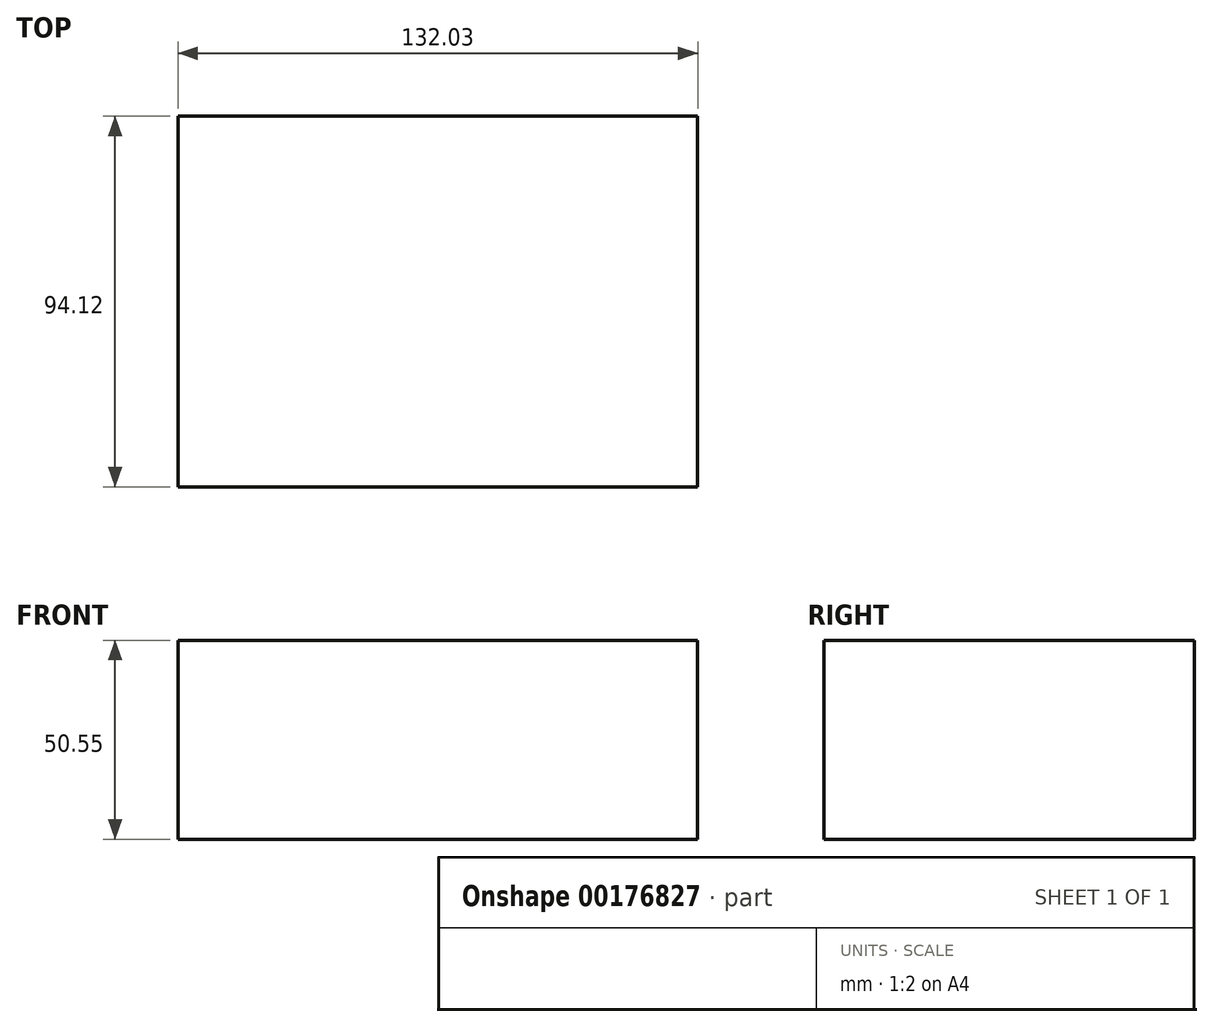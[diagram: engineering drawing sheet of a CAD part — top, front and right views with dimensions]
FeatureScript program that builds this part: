
annotation { "Feature Type Name" : "Feature", "Feature Type Description" : "" }
export const myFeature = defineFeature(function(context is Context, id is Id, definition is map)
    precondition{}
    {
        {
            var Q0;
            Q0=qCreatedBy(makeId("Top.planeOp"),FACE);
            var sketch = newSketch(context, id + "F0", { "sketchPlane" : qUnion([Q0])});
            skLineSegment(sketch, "E0.bottom", {"start": v(-87.33, 69.61) * mm, "end": v(44.7, 69.61) * mm});
            skLineSegment(sketch, "E0.top", {"start": v(-87.33, -24.5) * mm, "end": v(44.7, -24.5) * mm});
            skLineSegment(sketch, "E0.left", {"start": v(-87.33, 69.61) * mm, "end": v(-87.33, -24.5) * mm});
            skLineSegment(sketch, "E0.right", {"start": v(44.7, 69.61) * mm, "end": v(44.7, -24.5) * mm});
            skSolve(sketch);
        }
        {
            var Q0;
            Q0 = qSketchRegion(id + "F0", true);
            extrude(context, id + "F1", {"entities" : qUnion([Q0]), "depth" : 50.55 * mm});
        }
    });
